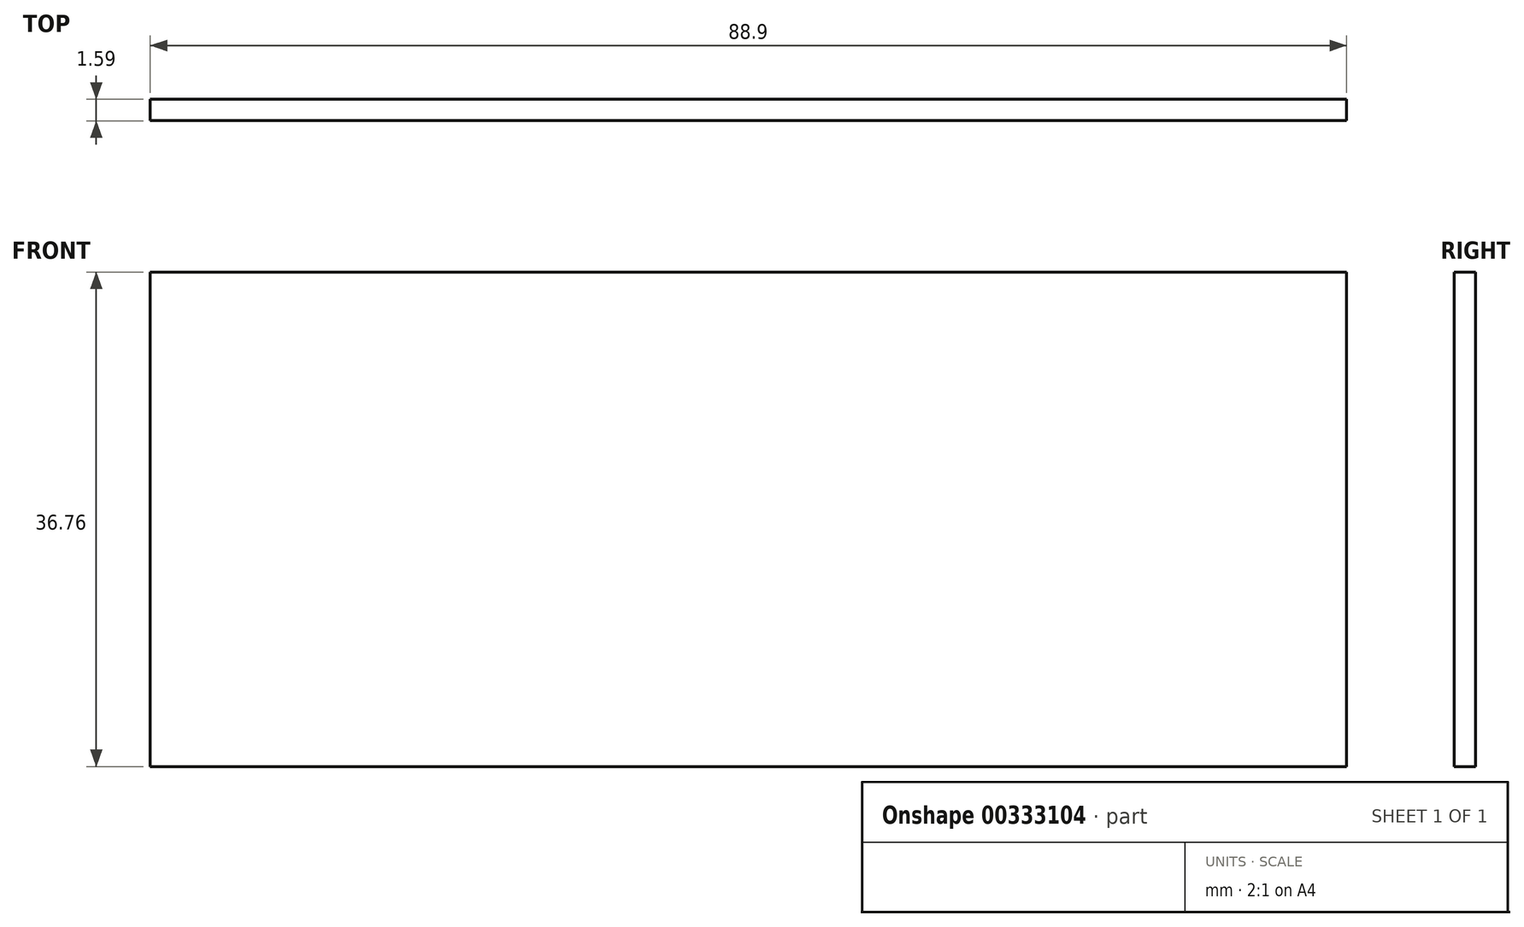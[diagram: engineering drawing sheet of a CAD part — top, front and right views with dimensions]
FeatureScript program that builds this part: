
annotation { "Feature Type Name" : "Feature", "Feature Type Description" : "" }
export const myFeature = defineFeature(function(context is Context, id is Id, definition is map)
    precondition{}
    {
        {
            var Q0;
            Q0=qCreatedBy(makeId("Front.planeOp"),FACE);
            var sketch = newSketch(context, id + "F0", { "sketchPlane" : qUnion([Q0])});
            skLineSegment(sketch, "E0.bottom", {"start": v(44.45, 18.38) * mm, "end": v(-44.45, 18.38) * mm});
            skLineSegment(sketch, "E0.top", {"start": v(44.45, -18.38) * mm, "end": v(-44.45, -18.38) * mm});
            skLineSegment(sketch, "E0.left", {"start": v(44.45, 18.38) * mm, "end": v(44.45, -18.38) * mm});
            skLineSegment(sketch, "E0.right", {"start": v(-44.45, 18.38) * mm, "end": v(-44.45, -18.38) * mm});
            skPoint(sketch, "E0.middle", {"position": v(0, 0) * mm});
            skSolve(sketch);
        }
        {
            var Q0;
            Q0=qSketchRegion(id+"F0",true);
            extrude(context, id + "F1", {"entities" : qUnion([Q0]), "depth" : 1.59 * mm});
        }
    });
